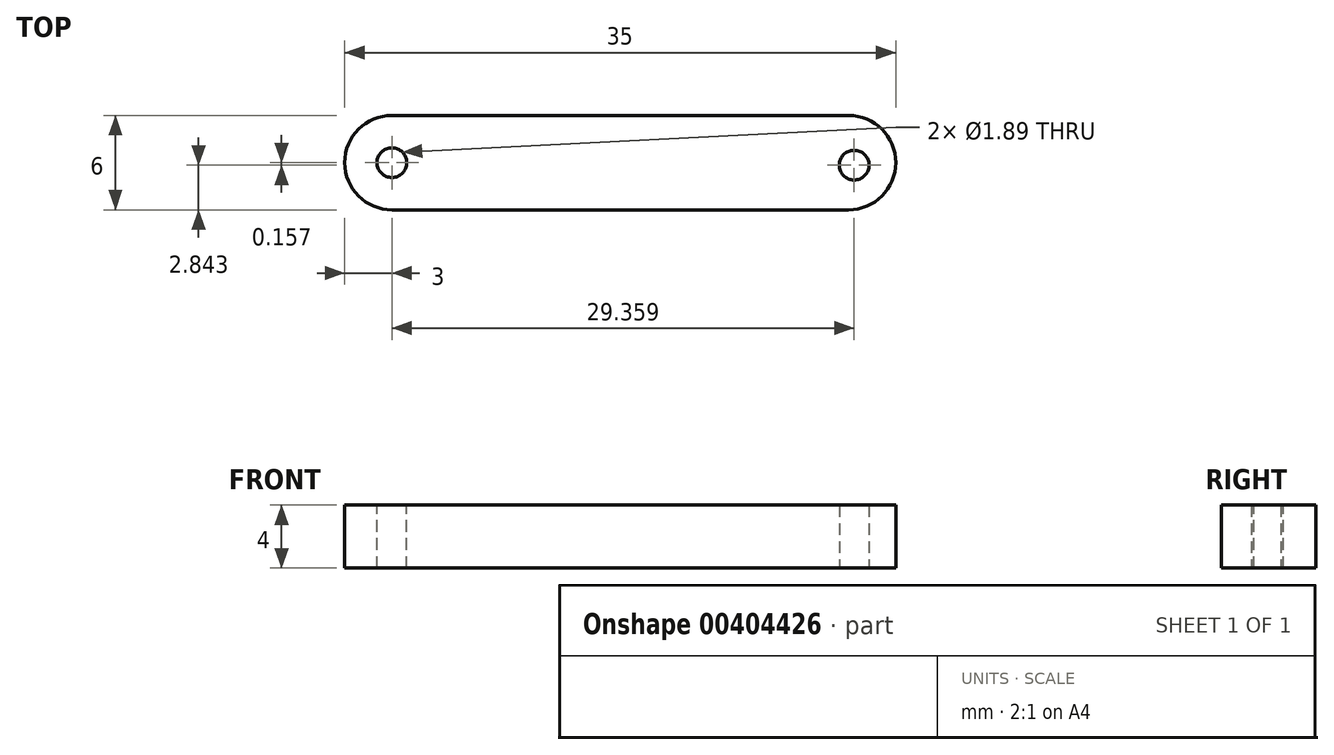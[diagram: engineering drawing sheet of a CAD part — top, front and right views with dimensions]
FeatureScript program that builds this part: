
annotation { "Feature Type Name" : "Feature", "Feature Type Description" : "" }
export const myFeature = defineFeature(function(context is Context, id is Id, definition is map)
    precondition{}
    {
        {
            var Q0;
            Q0=qCreatedBy(makeId("Top.planeOp"),FACE);
            var sketch = newSketch(context, id + "F0", { "sketchPlane" : qUnion([Q0])});
            skLineSegment(sketch, "E0", {"start": v(3, 0) * mm, "end": v(32, 0) * mm});
            skLineSegment(sketch, "E1", {"start": v(35, 3) * mm, "end": v(35, 3) * mm});
            skLineSegment(sketch, "E2", {"start": v(32, 6) * mm, "end": v(3, 6) * mm});
            skLineSegment(sketch, "E3", {"start": v(0, 3) * mm, "end": v(0, 3) * mm});
            skPoint(sketch, "E4.visualSharp", {"position": v(0, 0) * mm});
            skArc(sketch, "E4.filletArc", {"start": v(0, 3) * mm, "mid": v(0.88, 0.88) * mm, "end": v(3, 0) * mm});
            skPoint(sketch, "E5.visualSharp", {"position": v(35, 6) * mm});
            skArc(sketch, "E5.filletArc", {"start": v(35, 3) * mm, "mid": v(34.12, 5.12) * mm, "end": v(32, 6) * mm});
            skPoint(sketch, "E6.visualSharp", {"position": v(0, 6) * mm});
            skArc(sketch, "E6.filletArc", {"start": v(3, 6) * mm, "mid": v(0.88, 5.12) * mm, "end": v(0, 3) * mm});
            skPoint(sketch, "E7.visualSharp", {"position": v(35, 0) * mm});
            skArc(sketch, "E7.filletArc", {"start": v(32, 0) * mm, "mid": v(34.12, 0.88) * mm, "end": v(35, 3) * mm});
            skSolve(sketch);
        }
        {
            var Q0;
            Q0=makeQuery(id+"F0.imprint","IMPRINT",FACE,{"disambiguationData":[TD([[makeQuery(id+"F0.imprint","IMPRINT",EDGE,{"derivedFrom":sQuery(id+"F0.wireOp",EDGE,"E0")}),1.0]])]});
            extrude(context, id + "F1", {"entities" : qUnion([Q0]), "depth" : 4 * mm});
        }
        {
            var Q0;
            Q0=makeQuery(id+"F1.opExtrude","CAP_FACE",FACE,{"disambiguationData":[OSD([sQuery(id+"F0.wireOp",EDGE,"E0"),sQuery(id+"F0.wireOp",EDGE,"E2"),sQuery(id+"F0.wireOp",EDGE,"E4.filletArc"),sQuery(id+"F0.wireOp",EDGE,"E5.filletArc"),sQuery(id+"F0.wireOp",EDGE,"E6.filletArc"),sQuery(id+"F0.wireOp",EDGE,"E7.filletArc")])],"isStart":false});
            var sketch = newSketch(context, id + "F2", { "sketchPlane" : qUnion([Q0])});
            skCircle(sketch, "E8", {"center": v(3, 3) * mm, "radius": 0.94 * mm});
            skCircle(sketch, "E9", {"center": v(32, 3) * mm, "radius": 0.94 * mm});
            skSolve(sketch);
        }
        {
            var Q0;
            Q0=sQuery(id+"F2.wireOp",VERTEX,"E8.center");
            var Q1;
            Q1=makeQuery(id+"F1.opExtrude","SWEPT_BODY",BODY,{"disambiguationData":[OSD([sQuery(id+"F0.wireOp",EDGE,"E0"),sQuery(id+"F0.wireOp",EDGE,"E2"),sQuery(id+"F0.wireOp",EDGE,"E4.filletArc"),sQuery(id+"F0.wireOp",EDGE,"E5.filletArc"),sQuery(id+"F0.wireOp",EDGE,"E6.filletArc"),sQuery(id+"F0.wireOp",EDGE,"E7.filletArc")])]});
            hole(context, id + "F3", {"style" : HoleStyle.SIMPLE, "endStyle" : HoleEndStyle.THROUGH, "holeDiameter" : 1.89 * mm, "isTappedThrough" : true, "tappedDepth" : 12 * mm, "tapClearance" : 3, "locations" : qUnion([Q0]), "scope" : qUnion([Q1])});
        }
        {
            var Q0;
            Q0=qCreatedBy(makeId("Top.planeOp"),FACE);
            var sketch = newSketch(context, id + "F4", { "sketchPlane" : qUnion([Q0])});
            skCircle(sketch, "E10", {"center": v(32.36, 2.84) * mm, "radius": 0.94 * mm});
            skSolve(sketch);
        }
        {
            var Q0;
            Q0=sQuery(id+"F4.wireOp",VERTEX,"E10.center");
            var Q1;
            Q1=makeQuery(id+"F1.opExtrude","SWEPT_BODY",BODY,{"disambiguationData":[OSD([sQuery(id+"F0.wireOp",EDGE,"E0"),sQuery(id+"F0.wireOp",EDGE,"E2"),sQuery(id+"F0.wireOp",EDGE,"E4.filletArc"),sQuery(id+"F0.wireOp",EDGE,"E5.filletArc"),sQuery(id+"F0.wireOp",EDGE,"E6.filletArc"),sQuery(id+"F0.wireOp",EDGE,"E7.filletArc")])]});
            hole(context, id + "F5", {"style" : HoleStyle.SIMPLE, "endStyle" : HoleEndStyle.THROUGH, "oppositeDirection" : true, "holeDiameter" : 1.89 * mm, "isTappedThrough" : true, "tappedDepth" : 12 * mm, "tapClearance" : 3, "locations" : qUnion([Q0]), "scope" : qUnion([Q1])});
        }
    });
